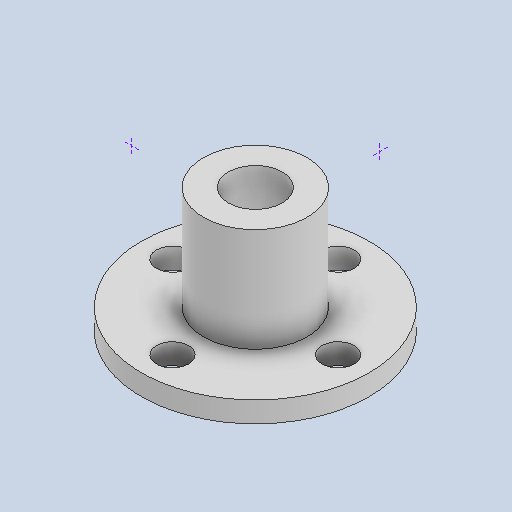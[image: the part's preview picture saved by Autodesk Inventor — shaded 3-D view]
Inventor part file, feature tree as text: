
AUTODESK INVENTOR PART (.ipt)
format: ipt  version: 2024.2 (Build 282272000, 272)  size: 248,320 bytes
history: native  units: mm
features: other x4, sketch x4, extrude x3
ambient origin geometry x8: Origin, YZ Plane, XZ Plane, XY Plane, X Axis, Y Axis, Z Axis, Center Point
bodies: Body1 (feature_tree)
feature tree (11):
  other  "Твердое тело1"
  sketch  "Эскиз1"
  extrude  "Выдавливание1"  Depth=5.2mm
  extrude  "Выдавливание2"  Depth=10.0mm
  sketch  "Эскиз2"
  sketch  "Эскиз3"
  other  "РабОсь4"
  other  "РабОсь5"
  other  "РабПлоскость1"
  extrude  "Выдавливание3"  Depth=22.0mm
  sketch  "Эскиз4"
